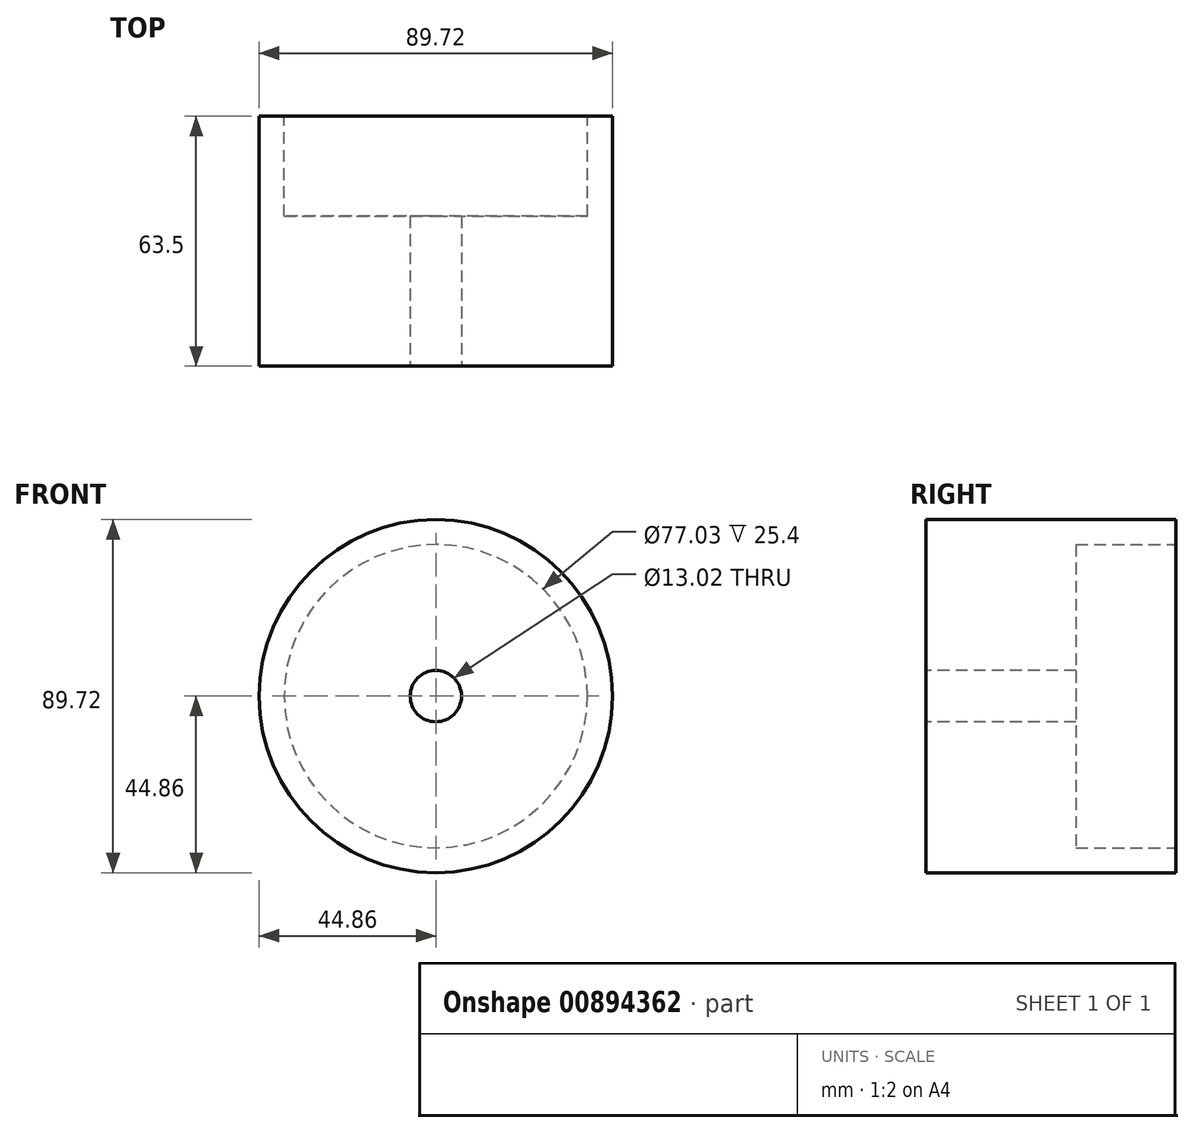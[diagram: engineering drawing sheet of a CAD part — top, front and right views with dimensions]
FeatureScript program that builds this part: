
annotation { "Feature Type Name" : "Feature", "Feature Type Description" : "" }
export const myFeature = defineFeature(function(context is Context, id is Id, definition is map)
    precondition{}
    {
        {
            var Q0;
            Q0=qCreatedBy(makeId("Front.planeOp"),FACE);
            var sketch = newSketch(context, id + "F0", { "sketchPlane" : qUnion([Q0])});
            skCircle(sketch, "E0", {"center": v(0, 0) * mm, "radius": 44.86 * mm});
            skSolve(sketch);
        }
        {
            var Q0;
            Q0 = qSketchRegion(id + "F0", true);
            extrude(context, id + "F1", {"entities" : qUnion([Q0]), "depth" : 63.5 * mm, "offsetDistance" : 25.4 * mm});
        }
        {
            var Q0;
            Q0=makeQuery(id+"F1.opExtrude","CAP_FACE",FACE,{"disambiguationData":[OSD([sQuery(id+"F0.wireOp",EDGE,"E0")])],"isStart":true});
            var sketch = newSketch(context, id + "F2", { "sketchPlane" : qUnion([Q0])});
            skCircle(sketch, "E1", {"center": v(0, 0) * mm, "radius": 38.52 * mm});
            skSolve(sketch);
        }
        {
            var Q0;
            Q0 = qSketchRegion(id + "F2", true);
            extrude(context, id + "F3", {"entities" : qUnion([Q0]), "operationType" : NewBodyOperationType.REMOVE, "oppositeDirection" : true, "depth" : 25.4 * mm, "offsetDistance" : 25.4 * mm});
        }
        {
            var Q0;
            Q0=makeQuery(id+"F1.opExtrude","CAP_FACE",FACE,{"disambiguationData":[OSD([sQuery(id+"F0.wireOp",EDGE,"E0")])],"isStart":false});
            var sketch = newSketch(context, id + "F4", { "sketchPlane" : qUnion([Q0])});
            skCircle(sketch, "E2", {"center": v(0, 0) * mm, "radius": 6.51 * mm});
            skSolve(sketch);
        }
        {
            var Q0;
            Q0 = qSketchRegion(id + "F4", true);
            extrude(context, id + "F5", {"entities" : qUnion([Q0]), "operationType" : NewBodyOperationType.REMOVE, "oppositeDirection" : true, "depth" : 63.5 * mm, "offsetDistance" : 25.4 * mm});
        }
    });
